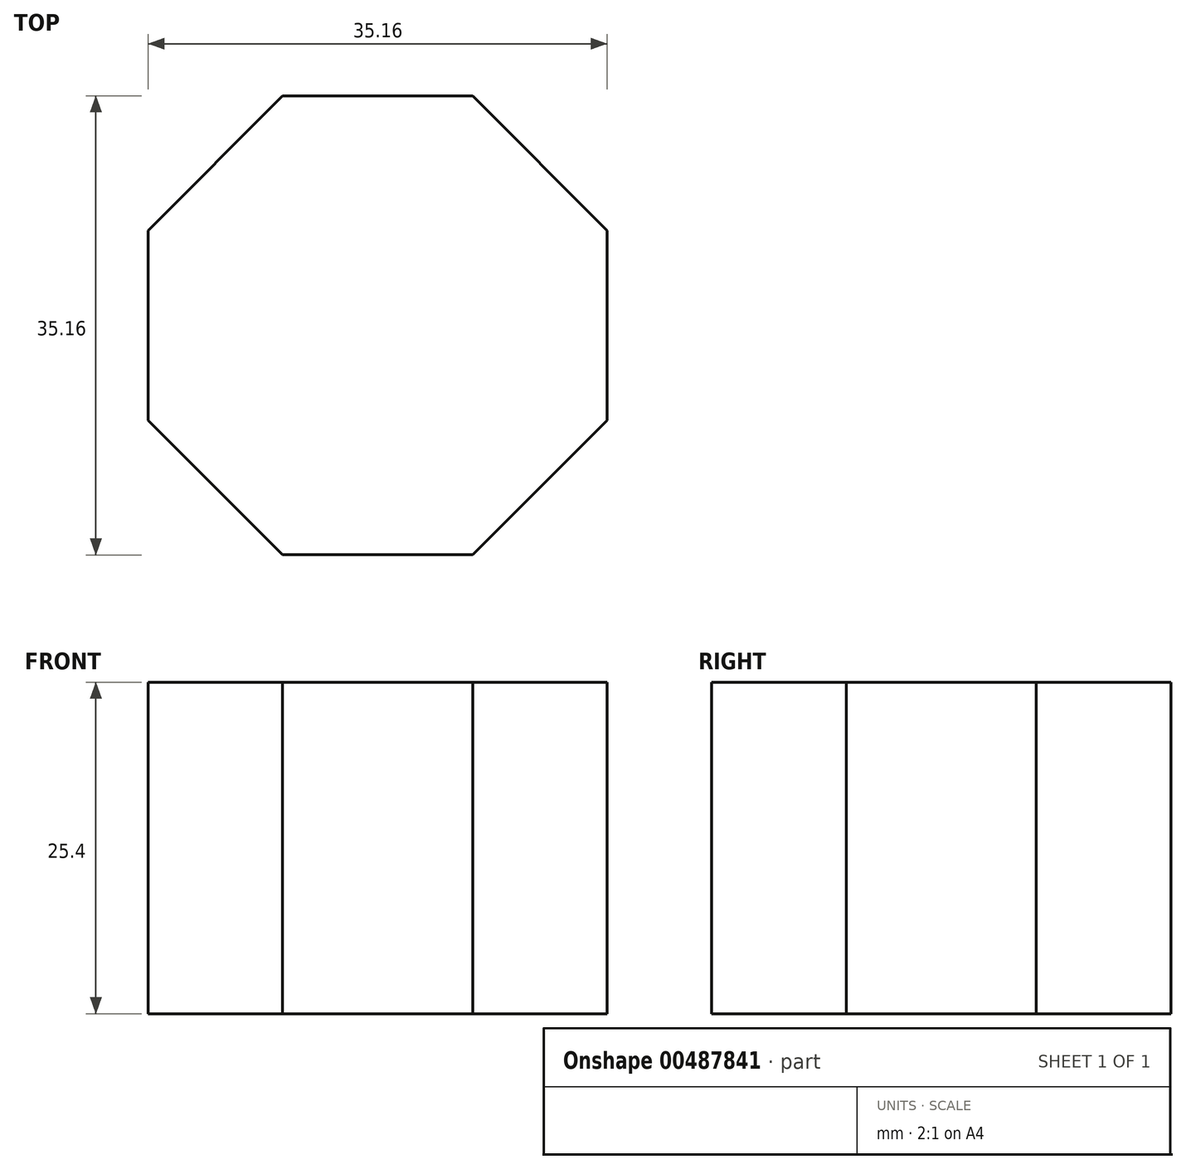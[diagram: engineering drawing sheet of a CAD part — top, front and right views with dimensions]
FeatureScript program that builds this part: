
annotation { "Feature Type Name" : "Feature", "Feature Type Description" : "" }
export const myFeature = defineFeature(function(context is Context, id is Id, definition is map)
    precondition{}
    {
        {
            var Q0;
            Q0=qCreatedBy(makeId("Top.planeOp"),FACE);
            var sketch = newSketch(context, id + "F0", { "sketchPlane" : qUnion([Q0])});
            skCircle(sketch, "E0.cCircle", {"center": v(0, 0) * mm, "radius": 17.58 * mm, "construction": true});
            skLineSegment(sketch, "E0.0", {"start": v(17.58, 7.28) * mm, "end": v(17.58, -7.28) * mm});
            skLineSegment(sketch, "E0.1", {"start": v(17.58, -7.28) * mm, "end": v(7.28, -17.58) * mm});
            skLineSegment(sketch, "E0.2", {"start": v(7.28, -17.58) * mm, "end": v(-7.28, -17.58) * mm});
            skLineSegment(sketch, "E0.3", {"start": v(-7.28, -17.58) * mm, "end": v(-17.58, -7.28) * mm});
            skLineSegment(sketch, "E0.4", {"start": v(-17.58, -7.28) * mm, "end": v(-17.58, 7.28) * mm});
            skLineSegment(sketch, "E0.5", {"start": v(-17.58, 7.28) * mm, "end": v(-7.28, 17.58) * mm});
            skLineSegment(sketch, "E0.6", {"start": v(-7.28, 17.58) * mm, "end": v(7.28, 17.58) * mm});
            skLineSegment(sketch, "E0.7", {"start": v(7.28, 17.58) * mm, "end": v(17.58, 7.28) * mm});
            skPoint(sketch, "E0.0.midPoint", {"position": v(17.58, 0) * mm});
            skSolve(sketch);
        }
        {
            var Q0;
            Q0=makeQuery(id+"F0.imprint","IMPRINT",FACE,{"disambiguationData":[TD([[makeQuery(id+"F0.imprint","IMPRINT",EDGE,{"derivedFrom":sQuery(id+"F0.wireOp",EDGE,"E0.0")}),-1.0]])]});
            extrude(context, id + "F1", {"entities" : qUnion([Q0]), "depth" : 25.4 * mm});
        }
        {
            var Q0;
            Q0=qCreatedBy(makeId("Top.planeOp"),FACE);
            var sketch = newSketch(context, id + "F2", { "sketchPlane" : qUnion([Q0])});
            skCircle(sketch, "E1.cCircle", {"center": v(0, 0) * mm, "radius": 12.76 * mm, "construction": true});
            skLineSegment(sketch, "E1.0", {"start": v(9.36, 10.62) * mm, "end": v(14.14, -0.7) * mm});
            skLineSegment(sketch, "E1.1", {"start": v(14.14, -0.7) * mm, "end": v(8.27, -11.5) * mm});
            skLineSegment(sketch, "E1.2", {"start": v(8.27, -11.5) * mm, "end": v(-3.83, -13.63) * mm});
            skLineSegment(sketch, "E1.3", {"start": v(-3.83, -13.63) * mm, "end": v(-13.05, -5.5) * mm});
            skLineSegment(sketch, "E1.4", {"start": v(-13.05, -5.5) * mm, "end": v(-12.44, 6.77) * mm});
            skLineSegment(sketch, "E1.5", {"start": v(-12.44, 6.77) * mm, "end": v(-2.46, 13.94) * mm});
            skLineSegment(sketch, "E1.6", {"start": v(-2.46, 13.94) * mm, "end": v(9.36, 10.62) * mm});
            skPoint(sketch, "E1.0.midPoint", {"position": v(11.75, 4.96) * mm});
            skSolve(sketch);
        }
        {
            var Q0;
            Q0 = qSketchRegion(id + "F2", true);
            extrude(context, id + "F3", {"entities" : qUnion([Q0]), "operationType" : NewBodyOperationType.ADD, "depth" : 25.4 * mm});
        }
    });
